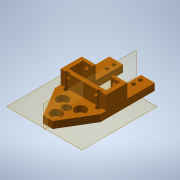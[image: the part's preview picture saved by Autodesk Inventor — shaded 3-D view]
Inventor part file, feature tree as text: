
AUTODESK INVENTOR PART (.ipt)
format: ipt  version: 2022 (Build 260153000, 153)  size: 350,720 bytes
history: native  units: mm
features: reference x21, other x14, sketch x10, extrude x9, plane x2, mirror x1, hole x1, projected_geometry x1
ambient origin geometry x8: Origin, YZ Plane, XZ Plane, XY Plane, X Axis, Y Axis, Z Axis, Center Point
bodies: Solid2 (feature_tree)
feature tree (59):
  plane  "Work Plane8"
  extrude  "Extrusion11"  Depth=5.0mm TaperAngle=0.0deg
  extrude  "Extrusion12"  Depth=10.0mm TaperAngle=0.0deg
  mirror  "Mirror3"
  extrude  "Extrusion16"  Depth=10.0mm TaperAngle=0.0deg
  extrude  "Extrusion17"  TaperAngle=0.0deg  [1 undecoded]
  hole  "Hole1"  [1 undecoded]
  extrude  "Extrusion18"  Depth=10.0mm TaperAngle=0.0deg
  extrude  "Extrusion19"  Depth=3.5mm
  extrude  "Extrusion21"  Depth=10.0mm
  extrude  "Extrusion22"  Depth=5.101063mm
  extrude  "Extrusion23"  Depth=10.0mm
  plane  "Arbeitsebene9"
  sketch  "Sketch12"  dims[d64=180.0deg d66=5.0mm d67=0.0mm]
  reference  "Reference33"
  reference  "Reference35"
  reference  "Reference36"
  sketch  "Sketch13"  dims[d70=10.0mm d71=0.0mm d83=4.5mm d84=0.0mm]
  reference  "Reference42"
  sketch  "Sketch17"  dims[d85=4.0mm d86=10.0mm d87=0.0mm]
  reference  "Reference44"
  reference  "Reference45"
  reference  "Reference46"
  sketch  "Sketch18"  dims[d89=3.2mm d90=6.0mm d91=6.0mm d92=22.0mm d93=90.0deg d94=8.0mm d95=20.594885mm d96=0.0mm]
  sketch  "Sketch19"  dims[d97=10.0mm d98=0.0mm d99=0.5mm]
  sketch  "Sketch20"  dims[d100=0.5mm d101=10.0mm d102=0.0mm]
  reference  "Reference50"
  reference  "Reference51"
  reference  "Reference52"
  reference  "Reference53"
  sketch  "Sketch21"  dims[d106=3.5mm d107=3.5mm]
  reference  "Reference54"
  sketch  "Sketch23"  dims[d108=10.0mm d109=0.0mm d110=0.3mm]
  reference  "Reference56"
  reference  "Reference57"
  reference  "Reference58"
  reference  "Reference59"
  reference  "Reference61"
  reference  "Reference63"
  reference  "Reference64"
  reference  "Reference65"
  sketch  "Skizze24"  dims[d111=0.3mm d114=5.101063mm]
  projected_geometry  "Projizierte Kontur11"
  sketch  "Skizze25"  dims[d115=6.998937mm d116=0.3mm d117=0.3mm d118=6.0mm d119=10.0mm d120=0.0mm d121=10.0mm d122=0.0mm d123=0.0mm]
  reference  "Referenz68"
  other  "Assembly_Cube_Z_Focus_Drylin_NEMA_v3.iam"
  other  "30_Cube_Z_Focus_MGN_NEMA_adapter:1"
  other  "30_Cube_Z_Focus_Drylin_NEMA_base_v3:1"
  other  "Assembly_Cube_Z_Focus_Drylin_NEMA_slide.iam"
  other  "30_Cube_Z_Focus_Drylin_NEMA_slide_part1:1"
  other  "30_Cube_Z_Focus_Drylin_NEMA_slide_part2:1"
  other  "Assembly_Cube_Z_Focus_MGN_NEMA_v3.iam"
  other  "30_Cube_Z_Focus_MGN_NEMA_adapter_RMS:1"
  other  "00_MGN12H, LINEAR GUIDE BLOCK:1"
  other  "00_NEMA11:1"
  other  "30_Cube_Z_Focus_MGN_NEMA_base_v3:1"
  other  "Assembly_Cube_empty_IM_v3:1"
  other  "10_Cube_1x1_IM:1"
  other  "30_Cube_Z_Focus_MGN_NEMA_rail:1"
note: 2 required parameter values undecoded (feature->parameter linkage not recoverable at this tier; creation-order binding heuristic only, values carry confidence <= 0.55)
